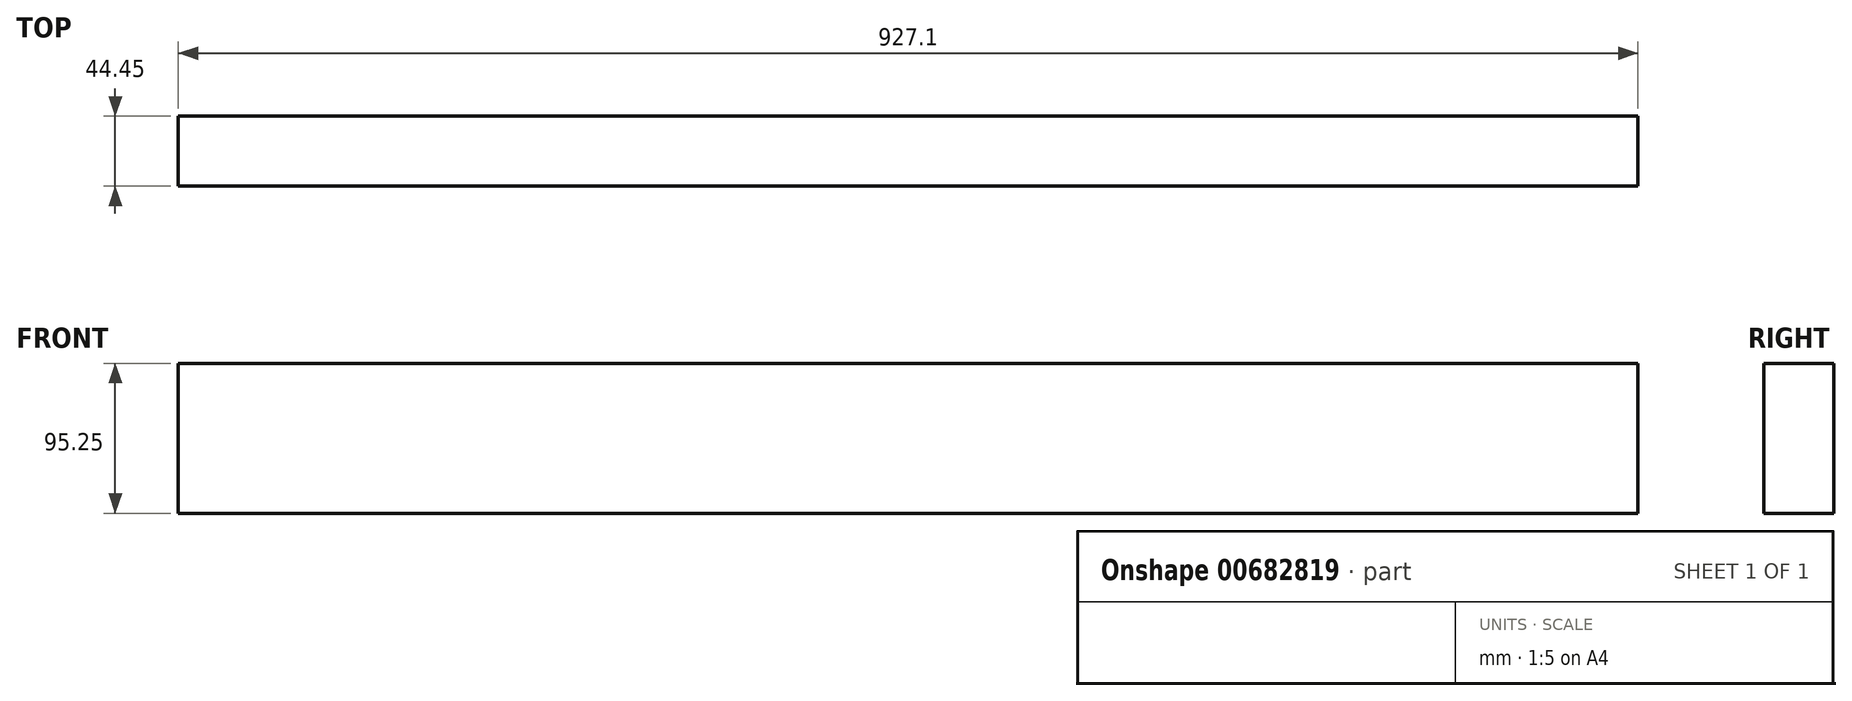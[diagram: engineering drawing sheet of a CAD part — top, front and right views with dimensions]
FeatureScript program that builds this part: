
annotation { "Feature Type Name" : "Feature", "Feature Type Description" : "" }
export const myFeature = defineFeature(function(context is Context, id is Id, definition is map)
    precondition{}
    {
        {
            var Q0;
            Q0=qCreatedBy(makeId("Front.planeOp"),FACE);
            var sketch = newSketch(context, id + "F0", { "sketchPlane" : qUnion([Q0])});
            skLineSegment(sketch, "E0.bottom", {"start": v(0, 0) * mm, "end": v(-927.1, 0) * mm});
            skLineSegment(sketch, "E0.top", {"start": v(0, 95.25) * mm, "end": v(-927.1, 95.25) * mm});
            skLineSegment(sketch, "E0.left", {"start": v(0, 0) * mm, "end": v(0, 95.25) * mm});
            skLineSegment(sketch, "E0.right", {"start": v(-927.1, 0) * mm, "end": v(-927.1, 95.25) * mm});
            skSolve(sketch);
        }
        {
            var Q0;
            Q0 = qSketchRegion(id + "F0", true);
            extrude(context, id + "F1", {"entities" : qUnion([Q0]), "depth" : 44.45 * mm, "offsetDistance" : 25.4 * mm});
        }
    });
